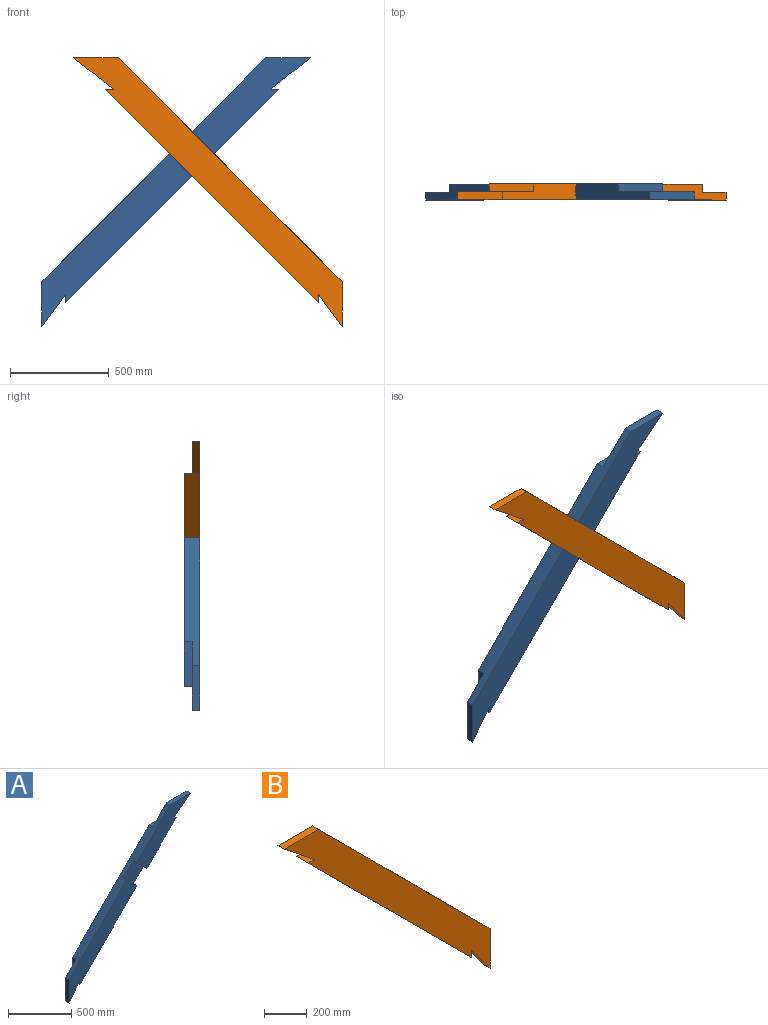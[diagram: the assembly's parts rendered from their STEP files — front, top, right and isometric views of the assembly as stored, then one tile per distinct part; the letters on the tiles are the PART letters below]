
ASSEMBLY  parts=2 mates=1
PART A: 16 faces, bbox 1360x80x1360 mm
  f0: plane 226.27x80mm, normal (-1,0,0), area 10748mm2, adj f1,f3,f4,f11,f14,f15
  f1: plane 1080x1080mm, normal (0.71,0,-0.71), area 115788.1mm2, adj f0,f2,f4,f5,f7,f9,f12,f15
  f2: plane 226.27x80mm, normal (0,0,1), area 10748mm2, adj f1,f3,f4,f8,f9,f10
  f3: plane 1133.73x1133.73mm, normal (-0.71,0,0.71), area 106027.2mm2, adj f0,f2,f4,f5,f6,f7,f9,f10
  f4: plane 1080x1080mm, normal (0,1,0), area 218776.1mm2, adj f0,f1,f2,f3
  f5: plane 226.27x226.27mm, normal (0,-1,0), area 25600mm2, adj f1,f3,f7,f12
  f6: plane 226.27x40mm, normal (0,0,1), area 9051mm2, adj f3,f8,f9,f10
  f7: plane 113.14x113.14mm, normal (-0.71,0,-0.71), area 6400mm2, adj f1,f3,f5,f9
  f8: plane 202.43x160mm, normal (0.62,0,-0.78), area 10321mm2, adj f2,f6,f9,f10
  f9: plane 600x486.86mm, normal (0,-1,0), area 93970.4mm2, adj f1,f2,f3,f6,f7,f8
  f10: plane 386.27x160mm, normal (0,1,0), area 32809.8mm2, adj f2,f3,f6,f8
  f11: plane 346.27x120mm, normal (0,1,0), area 24607.3mm2, adj f0,f3,f13,f14
  f12: plane 113.14x113.14mm, normal (0.71,0,0.71), area 6400mm2, adj f1,f3,f5,f15
  f13: plane 226.27x40mm, normal (-1,0,0), area 9051mm2, adj f3,f11,f14,f15
  f14: plane 162.43x120mm, normal (0.8,0,-0.59), area 8077.9mm2, adj f0,f11,f13,f15
  f15: plane 873.14x760mm, normal (0,-1,0), area 156622.8mm2, adj f0,f1,f3,f12,f13,f14
PART B: 16 faces, bbox 1360x80x1360 mm
  f0: plane 226.27x226.27mm, normal (0,1,0), area 25600mm2, adj f5,f9,f12,f14
  f1: plane 386.27x160mm, normal (0,1,0), area 32809.8mm2, adj f5,f6,f7,f8
  f2: plane 346.27x120mm, normal (0,1,0), area 24607.3mm2, adj f3,f4,f5,f10
  f3: plane 162.43x120mm, normal (-0.8,0,-0.59), area 8077.9mm2, adj f2,f4,f10,f11
  f4: plane 226.27x40mm, normal (1,0,0), area 9051mm2, adj f2,f3,f5,f11
  f5: plane 1133.73x1133.73mm, normal (0.71,0,0.71), area 106027.2mm2, adj f0,f1,f2,f4,f6,f8,f10,f11
  f6: plane 226.27x40mm, normal (0,0,1), area 9051mm2, adj f1,f5,f7,f11
  f7: plane 202.43x160mm, normal (-0.62,0,-0.78), area 10321mm2, adj f1,f6,f8,f11
  f8: plane 226.27x80mm, normal (0,0,1), area 10748mm2, adj f1,f5,f7,f9,f11,f13
  f9: plane 1080x1080mm, normal (-0.71,0,-0.71), area 115788.1mm2, adj f0,f8,f10,f11,f12,f13,f14,f15
  f10: plane 226.27x80mm, normal (1,0,0), area 10748mm2, adj f2,f3,f5,f9,f11,f15
  f11: plane 1360x1360mm, normal (0,-1,0), area 276193.2mm2, adj f3,f4,f5,f6,f7,f8,f9,f10
  f12: plane 113.14x113.14mm, normal (0.71,0,-0.71), area 6400mm2, adj f0,f5,f9,f13
  f13: plane 440x326.86mm, normal (0,1,0), area 61160.6mm2, adj f5,f8,f9,f12
  f14: plane 113.14x113.14mm, normal (-0.71,0,0.71), area 6400mm2, adj f0,f5,f9,f15
  f15: plane 753.14x640mm, normal (0,1,0), area 132015.5mm2, adj f5,f9,f10,f14
PLACE A t=(-520.75,282.81,-914.08)mm
PLACE B t=(-520.75,282.81,-914.08)mm
MATE fastened A.f5 <-> B.f0  axis (0,-1,0) through (-520.75,282.81,999.06)mm
